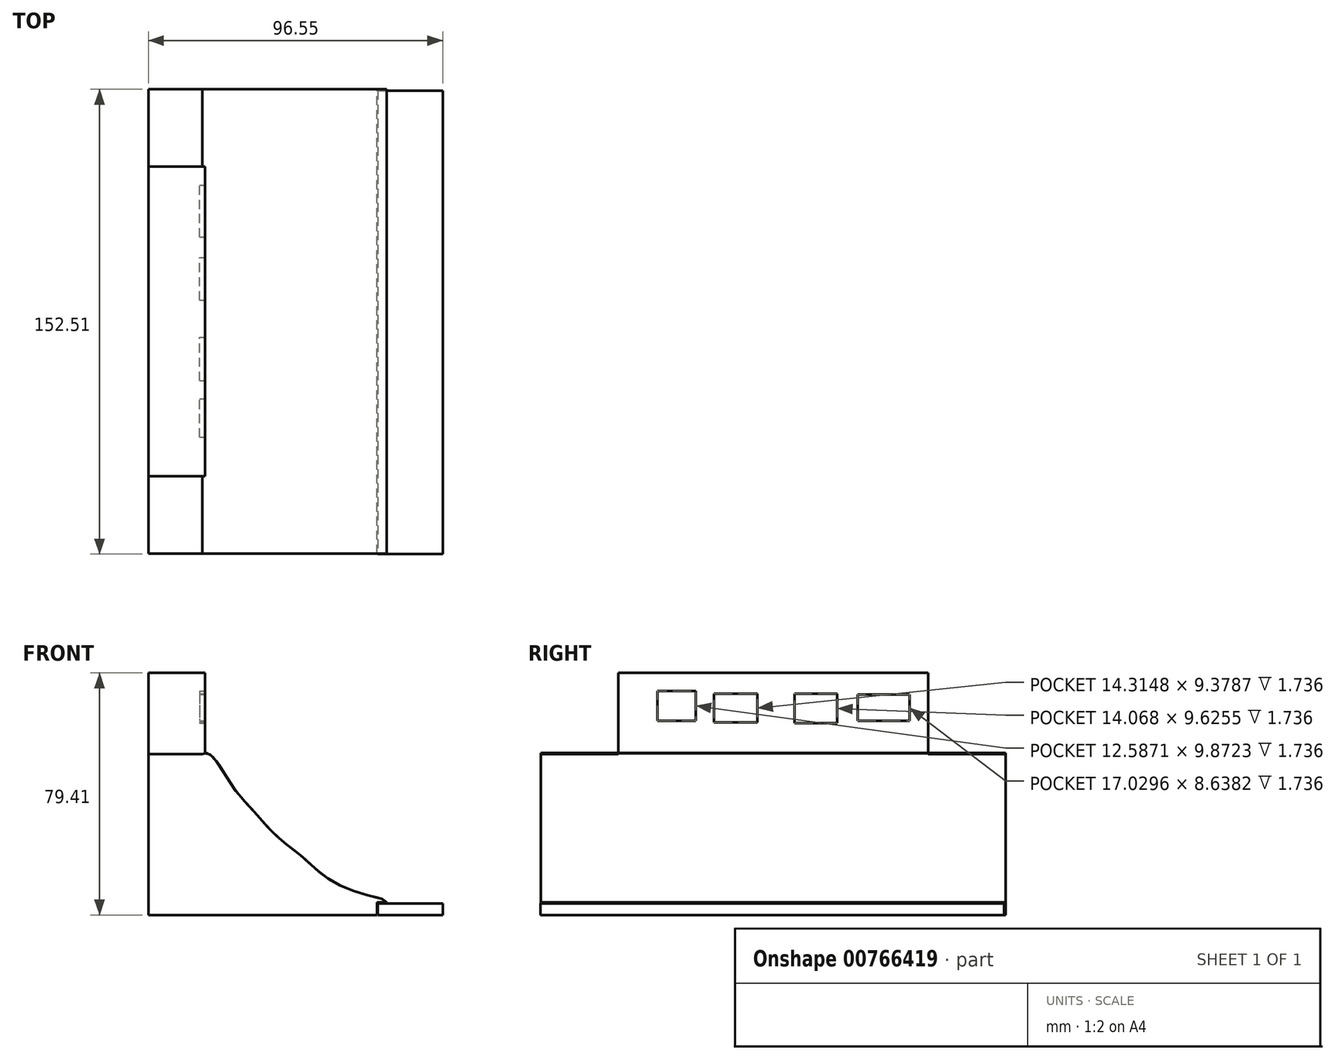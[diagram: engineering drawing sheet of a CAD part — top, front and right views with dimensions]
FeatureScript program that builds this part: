
annotation { "Feature Type Name" : "Feature", "Feature Type Description" : "" }
export const myFeature = defineFeature(function(context is Context, id is Id, definition is map)
    precondition{}
    {
        {
            var Q0;
            Q0=qCreatedBy(makeId("Top.planeOp"),FACE);
            var sketch = newSketch(context, id + "F0", { "sketchPlane" : qUnion([Q0])});
            skLineSegment(sketch, "E0.bottom", {"start": v(0, 75.77) * mm, "end": v(21.25, 75.77) * mm});
            skLineSegment(sketch, "E0.top", {"start": v(0, -76.3) * mm, "end": v(21.25, -76.3) * mm});
            skLineSegment(sketch, "E0.left", {"start": v(0, 75.77) * mm, "end": v(0, -76.3) * mm});
            skLineSegment(sketch, "E0.right", {"start": v(21.25, 75.77) * mm, "end": v(21.25, -76.3) * mm});
            skSolve(sketch);
        }
        {
            var Q0;
            Q0 = qSketchRegion(id + "F0", true);
            extrude(context, id + "F1", {"entities" : qUnion([Q0]), "depth" : 3.8 * mm, "offsetDistance" : 25.4 * mm});
        }
        {
            var Q0;
            Q0=qCreatedBy(makeId("Front.planeOp"),FACE);
            var sketch = newSketch(context, id + "F2", { "sketchPlane" : qUnion([Q0])});
            skLineSegment(sketch, "E1", {"start": v(-75.3, 52.82) * mm, "end": v(-57.65, 52.82) * mm});
            skFitSpline(sketch, "E2", {"points": [v(-57.65, 52.82) * mm, v(-55.23, 52.82) * mm, v(-47.98, 42.66) * mm, v(-42.42, 35.9) * mm, v(-33, 25.74) * mm, v(-25.26, 19.46) * mm, v(-13.66, 10.27) * mm, v(0, 5.64) * mm, v(2.85, 4.14) * mm], "startDerivative": vector(37.16, 12.91) * mm, "endDerivative": vector(44.23, -45.2) * mm});
            skLineSegment(sketch, "E3", {"start": v(-75.3, 52.82) * mm, "end": v(-75.3, 0) * mm});
            skLineSegment(sketch, "E4", {"start": v(2.85, 4.14) * mm, "end": v(0, 4.14) * mm});
            skLineSegment(sketch, "E5", {"start": v(0, 4.14) * mm, "end": v(-0.32, 4.14) * mm});
            skLineSegment(sketch, "E6", {"start": v(-0.32, 4.14) * mm, "end": v(-0.32, 0) * mm});
            skLineSegment(sketch, "E7", {"start": v(-0.32, 0) * mm, "end": v(-75.3, 0) * mm});
            skSolve(sketch);
        }
        {
            var Q0;
            Q0=makeQuery(id+"F2.imprint","IMPRINT",FACE,{"disambiguationData":[TD([[makeQuery(id+"F2.imprint","IMPRINT",EDGE,{"derivedFrom":sQuery(id+"F2.wireOp",EDGE,"E1")}),-1.0]])]});
            extrude(context, id + "F3", {"entities" : qUnion([Q0]), "operationType" : NewBodyOperationType.ADD, "depth" : 76.2 * mm, "offsetDistance" : 25.4 * mm});
        }
        {
            var Q0;
            Q0=makeQuery(id+"F3.opExtrude","CAP_FACE",FACE,{"disambiguationData":[OSD([sQuery(id+"F2.wireOp",EDGE,"E1"),sQuery(id+"F2.wireOp",EDGE,"E2"),sQuery(id+"F2.wireOp",EDGE,"E3"),sQuery(id+"F2.wireOp",EDGE,"zaHXE6N4-w8u5-yecR-uVTc-eUP8zXY4ykJm"),sQuery(id+"F2.wireOp",EDGE,"E4"),sQuery(id+"F2.wireOp",EDGE,"SJOHoY3i-YhUV-VHgw-RZLP-tTUyvz6DtQQF")])],"isStart":true});
            extrude(context, id + "F4", {"entities" : qUnion([Q0]), "operationType" : NewBodyOperationType.ADD, "depth" : 76.2 * mm, "offsetDistance" : 25.4 * mm});
        }
        {
            var Q0;
            Q0=qCreatedBy(makeId("Front.planeOp"),FACE);
            var sketch = newSketch(context, id + "F5", { "sketchPlane" : qUnion([Q0])});
            skLineSegment(sketch, "E8.bottom", {"start": v(-75.3, 52.82) * mm, "end": v(-56.68, 52.82) * mm});
            skLineSegment(sketch, "E8.top", {"start": v(-75.3, 79.4) * mm, "end": v(-56.68, 79.4) * mm});
            skLineSegment(sketch, "E8.left", {"start": v(-75.3, 52.82) * mm, "end": v(-75.3, 79.4) * mm});
            skLineSegment(sketch, "E8.right", {"start": v(-56.68, 52.82) * mm, "end": v(-56.68, 79.4) * mm});
            skSolve(sketch);
        }
        {
            var Q0;
            Q0=makeQuery(id+"F5.imprint","IMPRINT",FACE,{"disambiguationData":[TD([[makeQuery(id+"F5.imprint","IMPRINT",EDGE,{"derivedFrom":sQuery(id+"F5.wireOp",EDGE,"E8.bottom")}),1.0]])]});
            extrude(context, id + "F6", {"entities" : qUnion([Q0]), "operationType" : NewBodyOperationType.ADD, "depth" : 50.8 * mm, "offsetDistance" : 25.4 * mm});
        }
        {
            var Q0;
            Q0=makeQuery(id+"F6.opExtrude","CAP_FACE",FACE,{"disambiguationData":[OSD([sQuery(id+"F5.wireOp",EDGE,"E8.bottom"),sQuery(id+"F5.wireOp",EDGE,"E8.top"),sQuery(id+"F5.wireOp",EDGE,"E8.left"),sQuery(id+"F5.wireOp",EDGE,"E8.right")])],"isStart":true});
            extrude(context, id + "F7", {"entities" : qUnion([Q0]), "operationType" : NewBodyOperationType.ADD, "depth" : 50.8 * mm, "offsetDistance" : 25.4 * mm});
        }
        {
            var Q0;
            Q0=qCreatedBy(makeId("Right.planeOp"),FACE);
            var sketch = newSketch(context, id + "F8", { "sketchPlane" : qUnion([Q0])});
            skLineSegment(sketch, "E9.bottom", {"start": v(-37.94, 73.55) * mm, "end": v(-25.35, 73.55) * mm});
            skLineSegment(sketch, "E9.top", {"start": v(-37.94, 63.67) * mm, "end": v(-25.35, 63.67) * mm});
            skLineSegment(sketch, "E9.left", {"start": v(-37.94, 73.55) * mm, "end": v(-37.94, 63.67) * mm});
            skLineSegment(sketch, "E9.right", {"start": v(-25.35, 73.55) * mm, "end": v(-25.35, 63.67) * mm});
            skLineSegment(sketch, "E10.bottom", {"start": v(-19.43, 72.56) * mm, "end": v(-5.11, 72.56) * mm});
            skLineSegment(sketch, "E10.top", {"start": v(-19.43, 63.18) * mm, "end": v(-5.11, 63.18) * mm});
            skLineSegment(sketch, "E10.left", {"start": v(-19.43, 72.56) * mm, "end": v(-19.43, 63.18) * mm});
            skLineSegment(sketch, "E10.right", {"start": v(-5.11, 72.56) * mm, "end": v(-5.11, 63.18) * mm});
            skLineSegment(sketch, "E11.bottom", {"start": v(6.98, 72.56) * mm, "end": v(21.05, 72.56) * mm});
            skLineSegment(sketch, "E11.top", {"start": v(6.98, 62.93) * mm, "end": v(21.05, 62.93) * mm});
            skLineSegment(sketch, "E11.left", {"start": v(6.98, 72.56) * mm, "end": v(6.98, 62.93) * mm});
            skLineSegment(sketch, "E11.right", {"start": v(21.05, 72.56) * mm, "end": v(21.05, 62.93) * mm});
            skLineSegment(sketch, "E12.bottom", {"start": v(27.71, 72.31) * mm, "end": v(44.74, 72.31) * mm});
            skLineSegment(sketch, "E12.top", {"start": v(27.71, 63.67) * mm, "end": v(44.74, 63.67) * mm});
            skLineSegment(sketch, "E12.left", {"start": v(27.71, 72.31) * mm, "end": v(27.71, 63.67) * mm});
            skLineSegment(sketch, "E12.right", {"start": v(44.74, 72.31) * mm, "end": v(44.74, 63.67) * mm});
            skSolve(sketch);
        }
        {
            var Q0;
            Q0=makeQuery(id+"F8.imprint","IMPRINT",FACE,{"disambiguationData":[TD([[makeQuery(id+"F8.imprint","IMPRINT",EDGE,{"derivedFrom":sQuery(id+"F8.wireOp",EDGE,"E10.bottom")}),-1.0]])]});
            var Q1;
            Q1=makeQuery(id+"F8.imprint","IMPRINT",FACE,{"disambiguationData":[TD([[makeQuery(id+"F8.imprint","IMPRINT",EDGE,{"derivedFrom":sQuery(id+"F8.wireOp",EDGE,"E11.bottom")}),-1.0]])]});
            var Q2;
            Q2=makeQuery(id+"F8.imprint","IMPRINT",FACE,{"disambiguationData":[TD([[makeQuery(id+"F8.imprint","IMPRINT",EDGE,{"derivedFrom":sQuery(id+"F8.wireOp",EDGE,"E9.bottom")}),-1.0]])]});
            var Q3;
            Q3=makeQuery(id+"F8.imprint","IMPRINT",FACE,{"disambiguationData":[TD([[makeQuery(id+"F8.imprint","IMPRINT",EDGE,{"derivedFrom":sQuery(id+"F8.wireOp",EDGE,"E12.bottom")}),-1.0]])]});
            extrude(context, id + "F9", {"entities" : qUnion([Q0, Q1, Q2, Q3]), "operationType" : NewBodyOperationType.REMOVE, "oppositeDirection" : true, "depth" : 58.42 * mm, "offsetDistance" : 25.4 * mm});
        }
    });
